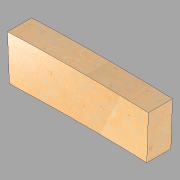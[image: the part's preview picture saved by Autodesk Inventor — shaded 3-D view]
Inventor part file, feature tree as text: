
AUTODESK INVENTOR PART (.ipt)
format: ipt  version: 2022.1 (Build 261234020, 234B)  size: 112,640 bytes
history: imported  units: in
note: dims shown in document units (in); Inventor stores cm internally (conversion verified against a paired STEP export)
features: imported_body x1
ambient origin geometry x8: Origin, YZ Plane, XZ Plane, XY Plane, X Axis, Y Axis, Z Axis, Center Point
bodies: Solid1 (imported_parasolid)
feature tree (1):
  imported_body  NMx_Import_Brep_tag  [imported B-rep: ~7 faces, bbox_mm=[891.325055, 281.320708, 152.4]]
